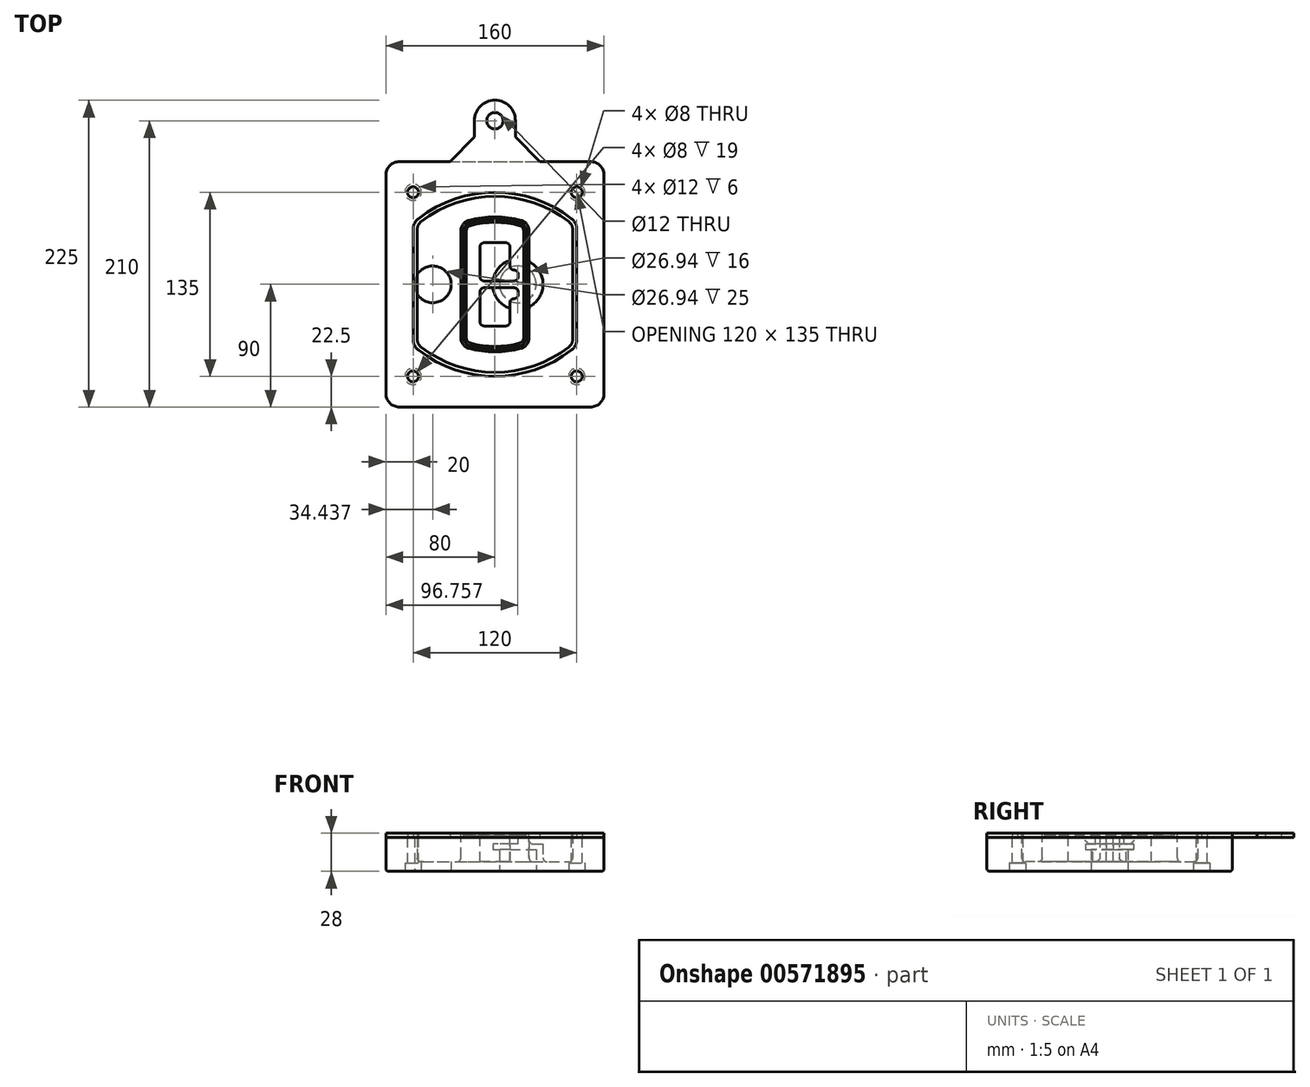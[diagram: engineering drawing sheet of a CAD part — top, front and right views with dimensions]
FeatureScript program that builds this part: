
annotation { "Feature Type Name" : "Feature", "Feature Type Description" : "" }
export const myFeature = defineFeature(function(context is Context, id is Id, definition is map)
    precondition{}
    {
        {
            var Q0;
            Q0=qCreatedBy(makeId("Top.planeOp"),FACE);
            var sketch = newSketch(context, id + "F0", { "sketchPlane" : qUnion([Q0])});
            skPoint(sketch, "E0.rect.middle", {"position": v(0, 0) * mm});
            skLineSegment(sketch, "E1.bottom", {"start": v(-70, -90) * mm, "end": v(70, -90) * mm});
            skLineSegment(sketch, "E1.top", {"start": v(-70, 90) * mm, "end": v(70, 90) * mm});
            skLineSegment(sketch, "E1.left", {"start": v(-80, -80) * mm, "end": v(-80, 80) * mm});
            skLineSegment(sketch, "E1.right", {"start": v(80, -80) * mm, "end": v(80, 80) * mm});
            skLineSegment(sketch, "E2", {"start": v(-80, 90) * mm, "end": v(80, -90) * mm, "construction": true});
            skLineSegment(sketch, "E3", {"start": v(80, 90) * mm, "end": v(-80, -90) * mm, "construction": true});
            skCircle(sketch, "E4", {"center": v(-60, 67.5) * mm, "radius": 4 * mm});
            skCircle(sketch, "E5", {"center": v(60, 67.5) * mm, "radius": 4 * mm});
            skCircle(sketch, "E6", {"center": v(60, -67.5) * mm, "radius": 4 * mm});
            skCircle(sketch, "E7", {"center": v(-60, -67.5) * mm, "radius": 4 * mm});
            skLineSegment(sketch, "E8", {"start": v(-60, 67.5) * mm, "end": v(60, 67.5) * mm, "construction": true});
            skLineSegment(sketch, "E9", {"start": v(60, 67.5) * mm, "end": v(60, -67.5) * mm, "construction": true});
            skLineSegment(sketch, "E10", {"start": v(60, -67.5) * mm, "end": v(-60, -67.5) * mm, "construction": true});
            skLineSegment(sketch, "E11", {"start": v(-60, -67.5) * mm, "end": v(-60, 67.5) * mm, "construction": true});
            skLineSegment(sketch, "E12", {"start": v(-60, 40.3) * mm, "end": v(-60, -40.3) * mm});
            skLineSegment(sketch, "E13", {"start": v(60, 40.3) * mm, "end": v(60, -40.3) * mm});
            skArc(sketch, "E14", {"start": v(56.15, 48.18) * mm, "mid": v(0, 67.5) * mm, "end": v(-56.15, 48.18) * mm});
            skArc(sketch, "E15", {"start": v(-56.15, -48.18) * mm, "mid": v(0, -67.5) * mm, "end": v(56.15, -48.18) * mm});
            skLineSegment(sketch, "E16", {"start": v(-60, 0) * mm, "end": v(60, 0) * mm, "construction": true});
            skPoint(sketch, "E17.visualSharp", {"position": v(-60, -45) * mm});
            skArc(sketch, "E17.filletArc", {"start": v(-60, -40.3) * mm, "mid": v(-58.99, -44.68) * mm, "end": v(-56.15, -48.18) * mm});
            skPoint(sketch, "E18.visualSharp", {"position": v(-60, 45) * mm});
            skArc(sketch, "E18.filletArc", {"start": v(-56.15, 48.18) * mm, "mid": v(-58.99, 44.68) * mm, "end": v(-60, 40.3) * mm});
            skPoint(sketch, "E19.visualSharp", {"position": v(60, 45) * mm});
            skArc(sketch, "E19.filletArc", {"start": v(60, 40.3) * mm, "mid": v(58.99, 44.68) * mm, "end": v(56.15, 48.18) * mm});
            skPoint(sketch, "E20.visualSharp", {"position": v(60, -45) * mm});
            skArc(sketch, "E20.filletArc", {"start": v(56.15, -48.18) * mm, "mid": v(58.99, -44.68) * mm, "end": v(60, -40.3) * mm});
            skPoint(sketch, "E21.visualSharp", {"position": v(-80, 90) * mm});
            skArc(sketch, "E21.filletArc", {"start": v(-70, 90) * mm, "mid": v(-77.07, 87.07) * mm, "end": v(-80, 80) * mm});
            skPoint(sketch, "E22.visualSharp", {"position": v(80, 90) * mm});
            skArc(sketch, "E22.filletArc", {"start": v(80, 80) * mm, "mid": v(77.07, 87.07) * mm, "end": v(70, 90) * mm});
            skPoint(sketch, "E23.visualSharp", {"position": v(80, -90) * mm});
            skArc(sketch, "E23.filletArc", {"start": v(70, -90) * mm, "mid": v(77.07, -87.07) * mm, "end": v(80, -80) * mm});
            skPoint(sketch, "E24.visualSharp", {"position": v(-80, -90) * mm});
            skArc(sketch, "E24.filletArc", {"start": v(-80, -80) * mm, "mid": v(-77.07, -87.07) * mm, "end": v(-70, -90) * mm});
            skArc(sketch, "E25.0", {"start": v(57, 40.3) * mm, "mid": v(56.3, 43.36) * mm, "end": v(54.3, 45.81) * mm});
            skLineSegment(sketch, "E25.1", {"start": v(57, 40.3) * mm, "end": v(57, -40.3) * mm});
            skArc(sketch, "E25.2", {"start": v(54.3, -45.81) * mm, "mid": v(56.3, -43.36) * mm, "end": v(57, -40.3) * mm});
            skArc(sketch, "E25.3", {"start": v(-54.3, -45.81) * mm, "mid": v(0, -64.5) * mm, "end": v(54.3, -45.81) * mm});
            skArc(sketch, "E25.4", {"start": v(-57, -40.3) * mm, "mid": v(-56.3, -43.36) * mm, "end": v(-54.3, -45.81) * mm});
            skArc(sketch, "E25.5", {"start": v(54.3, 45.81) * mm, "mid": v(0, 64.5) * mm, "end": v(-54.3, 45.81) * mm});
            skLineSegment(sketch, "E25.6", {"start": v(-57, 40.3) * mm, "end": v(-57, -40.3) * mm});
            skArc(sketch, "E25.7", {"start": v(-54.3, 45.81) * mm, "mid": v(-56.3, 43.36) * mm, "end": v(-57, 40.3) * mm});
            skArc(sketch, "E26.0", {"start": v(-58.62, 51.33) * mm, "mid": v(-62.58, 46.43) * mm, "end": v(-64, 40.3) * mm});
            skArc(sketch, "E26.1", {"start": v(58.62, 51.33) * mm, "mid": v(0, 71.5) * mm, "end": v(-58.62, 51.33) * mm});
            skArc(sketch, "E26.2", {"start": v(64, 40.3) * mm, "mid": v(62.58, 46.43) * mm, "end": v(58.62, 51.33) * mm});
            skLineSegment(sketch, "E26.3", {"start": v(64, 40.3) * mm, "end": v(64, -40.3) * mm});
            skArc(sketch, "E26.4", {"start": v(58.62, -51.33) * mm, "mid": v(62.58, -46.43) * mm, "end": v(64, -40.3) * mm});
            skLineSegment(sketch, "E26.5", {"start": v(-64, 40.3) * mm, "end": v(-64, -40.3) * mm});
            skArc(sketch, "E26.6", {"start": v(-58.62, -51.33) * mm, "mid": v(0, -71.5) * mm, "end": v(58.62, -51.33) * mm});
            skArc(sketch, "E26.7", {"start": v(-64, -40.3) * mm, "mid": v(-62.58, -46.43) * mm, "end": v(-58.62, -51.33) * mm});
            skSolve(sketch);
        }
        {
            var Q0;
            Q0=makeQuery(id+"F0.imprint","IMPRINT",FACE,{"disambiguationData":[TD([[makeQuery(id+"F0.imprint","IMPRINT",EDGE,{"derivedFrom":sQuery(id+"F0.wireOp",EDGE,"E1.bottom")}),1.0]])]});
            var Q1;
            Q1=makeQuery(id+"F0.imprint","IMPRINT",FACE,{"disambiguationData":[TD([[makeQuery(id+"F0.imprint","IMPRINT",EDGE,{"derivedFrom":sQuery(id+"F0.wireOp",EDGE,"E12")}),1.0]])]});
            var Q2;
            Q2=makeQuery(id+"F0.imprint","IMPRINT",FACE,{"disambiguationData":[TD([[makeQuery(id+"F0.imprint","IMPRINT",EDGE,{"derivedFrom":sQuery(id+"F0.wireOp",EDGE,"E25.0")}),1.0]])]});
            var Q3;
            Q3=makeQuery(id+"F0.imprint","IMPRINT",FACE,{"disambiguationData":[TD([[makeQuery(id+"F0.imprint","IMPRINT",EDGE,{"derivedFrom":sQuery(id+"F0.wireOp",EDGE,"E12")}),-1.0]])]});
            extrude(context, id + "F1", {"entities" : qUnion([Q0, Q1, Q2, Q3]), "oppositeDirection" : true, "depth" : 25 * mm});
        }
        {
            var Q0;
            Q0=makeQuery(id+"F0.imprint","IMPRINT",FACE,{"disambiguationData":[TD([[makeQuery(id+"F0.imprint","IMPRINT",EDGE,{"derivedFrom":sQuery(id+"F0.wireOp",EDGE,"E12")}),1.0]])]});
            extrude(context, id + "F2", {"entities" : qUnion([Q0]), "operationType" : NewBodyOperationType.ADD, "depth" : 3 * mm});
        }
        {
            var Q0;
            Q0=makeQuery(id+"F0.imprint","IMPRINT",FACE,{"disambiguationData":[TD([[makeQuery(id+"F0.imprint","IMPRINT",EDGE,{"derivedFrom":sQuery(id+"F0.wireOp",EDGE,"E25.0")}),1.0]])]});
            extrude(context, id + "F3", {"entities" : qUnion([Q0]), "operationType" : NewBodyOperationType.REMOVE, "oppositeDirection" : true, "depth" : 18 * mm});
        }
        {
            var Q0;
            Q0=makeQuery(id+"F2.opExtrude","CAP_FACE",FACE,{"disambiguationData":[OSD([sQuery(id+"F0.wireOp",EDGE,"E12"),sQuery(id+"F0.wireOp",EDGE,"E13"),sQuery(id+"F0.wireOp",EDGE,"E14"),sQuery(id+"F0.wireOp",EDGE,"E15"),sQuery(id+"F0.wireOp",EDGE,"E17.filletArc"),sQuery(id+"F0.wireOp",EDGE,"E18.filletArc"),sQuery(id+"F0.wireOp",EDGE,"E19.filletArc"),sQuery(id+"F0.wireOp",EDGE,"E20.filletArc"),sQuery(id+"F0.wireOp",EDGE,"E25.0"),sQuery(id+"F0.wireOp",EDGE,"E25.1"),sQuery(id+"F0.wireOp",EDGE,"E25.2"),sQuery(id+"F0.wireOp",EDGE,"E25.3"),sQuery(id+"F0.wireOp",EDGE,"E25.4"),sQuery(id+"F0.wireOp",EDGE,"E25.5"),sQuery(id+"F0.wireOp",EDGE,"E25.6"),sQuery(id+"F0.wireOp",EDGE,"E25.7")])],"isStart":false});
            var sketch = newSketch(context, id + "F4", { "sketchPlane" : qUnion([Q0])});
            skArc(sketch, "E27.0", {"start": v(-19.08, -46.97) * mm, "mid": v(0, -49.5) * mm, "end": v(19.08, -46.97) * mm});
            skArc(sketch, "E28.0", {"start": v(19.08, 46.97) * mm, "mid": v(0, 49.5) * mm, "end": v(-19.08, 46.97) * mm});
            skLineSegment(sketch, "E29", {"start": v(-25, 39.25) * mm, "end": v(-25, -39.25) * mm});
            skLineSegment(sketch, "E30", {"start": v(25, 39.25) * mm, "end": v(25, -39.25) * mm});
            skLineSegment(sketch, "E31", {"start": v(-25, 45.1) * mm, "end": v(25, 45.1) * mm, "construction": true});
            skLineSegment(sketch, "E32", {"start": v(-25, -45.1) * mm, "end": v(25, -45.1) * mm, "construction": true});
            skPoint(sketch, "E33.visualSharp", {"position": v(-25, 45.1) * mm});
            skArc(sketch, "E33.filletArc", {"start": v(-19.08, 46.97) * mm, "mid": v(-23.35, 44.11) * mm, "end": v(-25, 39.25) * mm});
            skPoint(sketch, "E34.visualSharp", {"position": v(25, 45.1) * mm});
            skArc(sketch, "E34.filletArc", {"start": v(25, 39.25) * mm, "mid": v(23.35, 44.11) * mm, "end": v(19.08, 46.97) * mm});
            skPoint(sketch, "E35.visualSharp", {"position": v(25, -45.1) * mm});
            skArc(sketch, "E35.filletArc", {"start": v(19.08, -46.97) * mm, "mid": v(23.35, -44.11) * mm, "end": v(25, -39.25) * mm});
            skPoint(sketch, "E36.visualSharp", {"position": v(-25, -45.1) * mm});
            skArc(sketch, "E36.filletArc", {"start": v(-25, -39.25) * mm, "mid": v(-23.35, -44.11) * mm, "end": v(-19.08, -46.97) * mm});
            skArc(sketch, "E37.0", {"start": v(54.3, 45.81) * mm, "mid": v(0, 64.5) * mm, "end": v(-54.3, 45.81) * mm});
            skArc(sketch, "E37.1", {"start": v(-54.3, 45.81) * mm, "mid": v(-56.3, 43.36) * mm, "end": v(-57, 40.3) * mm});
            skLineSegment(sketch, "E37.2", {"start": v(-57, 40.3) * mm, "end": v(-57, -40.3) * mm});
            skArc(sketch, "E37.3", {"start": v(-57, -40.3) * mm, "mid": v(-56.3, -43.36) * mm, "end": v(-54.3, -45.81) * mm});
            skArc(sketch, "E37.4", {"start": v(-54.3, -45.81) * mm, "mid": v(0, -64.5) * mm, "end": v(54.3, -45.81) * mm});
            skArc(sketch, "E37.5", {"start": v(54.3, -45.81) * mm, "mid": v(56.3, -43.36) * mm, "end": v(57, -40.3) * mm});
            skLineSegment(sketch, "E37.6", {"start": v(57, 40.3) * mm, "end": v(57, -40.3) * mm});
            skArc(sketch, "E37.7", {"start": v(57, 40.3) * mm, "mid": v(56.3, 43.36) * mm, "end": v(54.3, 45.81) * mm});
            skLineSegment(sketch, "E38.0", {"start": v(23, 39.25) * mm, "end": v(23, -39.25) * mm});
            skArc(sketch, "E38.1", {"start": v(18.56, -45.04) * mm, "mid": v(21.76, -42.9) * mm, "end": v(23, -39.25) * mm});
            skArc(sketch, "E38.2", {"start": v(-18.56, -45.04) * mm, "mid": v(0, -47.5) * mm, "end": v(18.56, -45.04) * mm});
            skArc(sketch, "E38.3", {"start": v(-23, -39.25) * mm, "mid": v(-21.76, -42.9) * mm, "end": v(-18.56, -45.04) * mm});
            skLineSegment(sketch, "E38.4", {"start": v(-23, 39.25) * mm, "end": v(-23, -39.25) * mm});
            skArc(sketch, "E38.5", {"start": v(23, 39.25) * mm, "mid": v(21.76, 42.9) * mm, "end": v(18.56, 45.04) * mm});
            skArc(sketch, "E38.6", {"start": v(-18.56, 45.04) * mm, "mid": v(-21.76, 42.9) * mm, "end": v(-23, 39.25) * mm});
            skArc(sketch, "E38.7", {"start": v(18.56, 45.04) * mm, "mid": v(0, 47.5) * mm, "end": v(-18.56, 45.04) * mm});
            skArc(sketch, "E39.0", {"start": v(21, 39.25) * mm, "mid": v(20.18, 41.68) * mm, "end": v(18.04, 43.1) * mm});
            skLineSegment(sketch, "E39.1", {"start": v(21, 39.25) * mm, "end": v(21, -39.25) * mm});
            skArc(sketch, "E39.2", {"start": v(18.04, -43.1) * mm, "mid": v(20.18, -41.68) * mm, "end": v(21, -39.25) * mm});
            skArc(sketch, "E39.3", {"start": v(-18.04, -43.1) * mm, "mid": v(0, -45.5) * mm, "end": v(18.04, -43.1) * mm});
            skArc(sketch, "E39.4", {"start": v(-21, -39.25) * mm, "mid": v(-20.18, -41.68) * mm, "end": v(-18.04, -43.1) * mm});
            skArc(sketch, "E39.5", {"start": v(18.04, 43.1) * mm, "mid": v(0, 45.5) * mm, "end": v(-18.04, 43.1) * mm});
            skLineSegment(sketch, "E39.6", {"start": v(-21, 39.25) * mm, "end": v(-21, -39.25) * mm});
            skArc(sketch, "E39.7", {"start": v(-18.04, 43.1) * mm, "mid": v(-20.18, 41.68) * mm, "end": v(-21, 39.25) * mm});
            skLineSegment(sketch, "E40", {"start": v(-25, 0) * mm, "end": v(25, 0) * mm, "construction": true});
            skLineSegment(sketch, "E41", {"start": v(-11, 5.5) * mm, "end": v(-11, 27.5) * mm});
            skLineSegment(sketch, "E42", {"start": v(-8, 30.5) * mm, "end": v(8, 30.5) * mm});
            skLineSegment(sketch, "E43", {"start": v(11, 27.5) * mm, "end": v(11, 13.5) * mm});
            skLineSegment(sketch, "E44", {"start": v(14, 10.5) * mm, "end": v(14, 10.5) * mm});
            skLineSegment(sketch, "E45", {"start": v(17, 7.5) * mm, "end": v(17, 5.5) * mm});
            skLineSegment(sketch, "E46", {"start": v(14, 2.5) * mm, "end": v(-8, 2.5) * mm});
            skPoint(sketch, "E47.visualSharp", {"position": v(-11, 30.5) * mm});
            skArc(sketch, "E47.filletArc", {"start": v(-8, 30.5) * mm, "mid": v(-10.12, 29.62) * mm, "end": v(-11, 27.5) * mm});
            skPoint(sketch, "E48.visualSharp", {"position": v(11, 30.5) * mm});
            skArc(sketch, "E48.filletArc", {"start": v(11, 27.5) * mm, "mid": v(10.12, 29.62) * mm, "end": v(8, 30.5) * mm});
            skPoint(sketch, "E49.visualSharp", {"position": v(11, 10.5) * mm});
            skArc(sketch, "E49.filletArc", {"start": v(11, 13.5) * mm, "mid": v(11.88, 11.38) * mm, "end": v(14, 10.5) * mm});
            skPoint(sketch, "E50.visualSharp", {"position": v(17, 10.5) * mm});
            skArc(sketch, "E50.filletArc", {"start": v(17, 7.5) * mm, "mid": v(16.12, 9.62) * mm, "end": v(14, 10.5) * mm});
            skPoint(sketch, "E51.visualSharp", {"position": v(17, 2.5) * mm});
            skArc(sketch, "E51.filletArc", {"start": v(14, 2.5) * mm, "mid": v(16.12, 3.38) * mm, "end": v(17, 5.5) * mm});
            skPoint(sketch, "E52.visualSharp", {"position": v(-11, 2.5) * mm});
            skArc(sketch, "E52.filletArc", {"start": v(-11, 5.5) * mm, "mid": v(-10.12, 3.38) * mm, "end": v(-8, 2.5) * mm});
            skLineSegment(sketch, "E53.0.MirrorCS", {"start": v(14, -2.5) * mm, "end": v(-8, -2.5) * mm});
            skArc(sketch, "E54.0.MirrorCS", {"start": v(-11, -5.5) * mm, "mid": v(-10.12, -3.38) * mm, "end": v(-8, -2.5) * mm});
            skLineSegment(sketch, "E55.0.MirrorCS", {"start": v(-11, -5.5) * mm, "end": v(-11, -27.5) * mm});
            skArc(sketch, "E56.0.MirrorCS", {"start": v(-8, -30.5) * mm, "mid": v(-10.12, -29.62) * mm, "end": v(-11, -27.5) * mm});
            skLineSegment(sketch, "E57.0.MirrorCS", {"start": v(-8, -30.5) * mm, "end": v(8, -30.5) * mm});
            skArc(sketch, "E58.0.MirrorCS", {"start": v(11, -27.5) * mm, "mid": v(10.12, -29.62) * mm, "end": v(8, -30.5) * mm});
            skLineSegment(sketch, "E59.0.MirrorCS", {"start": v(11, -27.5) * mm, "end": v(11, -13.5) * mm});
            skArc(sketch, "E60.0.MirrorCS", {"start": v(11, -13.5) * mm, "mid": v(11.88, -11.38) * mm, "end": v(14, -10.5) * mm});
            skArc(sketch, "E61.0.MirrorCS", {"start": v(17, -7.5) * mm, "mid": v(16.12, -9.62) * mm, "end": v(14, -10.5) * mm});
            skLineSegment(sketch, "E62.0.MirrorCS", {"start": v(17, -7.5) * mm, "end": v(17, -5.5) * mm});
            skArc(sketch, "E63.0.MirrorCS", {"start": v(14, -2.5) * mm, "mid": v(16.12, -3.38) * mm, "end": v(17, -5.5) * mm});
            skSolve(sketch);
        }
        {
            var Q0;
            Q0=makeQuery(id+"F4.imprint","IMPRINT",FACE,{"disambiguationData":[TD([[makeQuery(id+"F4.imprint","IMPRINT",EDGE,{"derivedFrom":sQuery(id+"F4.wireOp",EDGE,"E27.0")}),1.0]])]});
            var Q1;
            Q1=makeQuery(id+"F4.imprint","IMPRINT",FACE,{"disambiguationData":[TD([[makeQuery(id+"F4.imprint","IMPRINT",EDGE,{"derivedFrom":sQuery(id+"F4.wireOp",EDGE,"E38.0")}),-1.0]])]});
            var Q2;
            Q2=makeQuery(id+"F4.imprint","IMPRINT",FACE,{"disambiguationData":[TD([[makeQuery(id+"F4.imprint","IMPRINT",EDGE,{"derivedFrom":sQuery(id+"F4.wireOp",EDGE,"E39.0")}),1.0]])]});
            extrude(context, id + "F5", {"entities" : qUnion([Q0, Q1, Q2]), "operationType" : NewBodyOperationType.ADD, "endBound" : BoundingType.UP_TO_NEXT, "oppositeDirection" : true, "depth" : 25 * mm});
        }
        {
            var Q0;
            Q0=makeQuery(id+"F4.imprint","IMPRINT",FACE,{"disambiguationData":[TD([[makeQuery(id+"F4.imprint","IMPRINT",EDGE,{"derivedFrom":sQuery(id+"F4.wireOp",EDGE,"E38.0")}),-1.0]])]});
            extrude(context, id + "F6", {"entities" : qUnion([Q0]), "operationType" : NewBodyOperationType.REMOVE, "oppositeDirection" : true, "depth" : 2 * mm});
        }
        {
            var Q0;
            Q0=makeQuery(id+"F1.opExtrude","CAP_FACE",FACE,{"disambiguationData":[OSD([sQuery(id+"F0.wireOp",EDGE,"E1.bottom"),sQuery(id+"F0.wireOp",EDGE,"E1.top"),sQuery(id+"F0.wireOp",EDGE,"E1.left"),sQuery(id+"F0.wireOp",EDGE,"E1.right"),sQuery(id+"F0.wireOp",EDGE,"E4"),sQuery(id+"F0.wireOp",EDGE,"E5"),sQuery(id+"F0.wireOp",EDGE,"E6"),sQuery(id+"F0.wireOp",EDGE,"E7"),sQuery(id+"F0.wireOp",EDGE,"E21.filletArc"),sQuery(id+"F0.wireOp",EDGE,"E22.filletArc"),sQuery(id+"F0.wireOp",EDGE,"E23.filletArc"),sQuery(id+"F0.wireOp",EDGE,"E24.filletArc")])],"isStart":false});
            var sketch = newSketch(context, id + "F7", { "sketchPlane" : qUnion([Q0])});
            skCircle(sketch, "E64", {"center": v(16.76, 0) * mm, "radius": 13.47 * mm});
            skCircle(sketch, "E65", {"center": v(-45.56, 0) * mm, "radius": 13.47 * mm});
            skLineSegment(sketch, "E66", {"start": v(80, 0) * mm, "end": v(-80, 0) * mm});
            skCircle(sketch, "E67", {"center": v(16.76, 0) * mm, "radius": 18.47 * mm});
            skCircle(sketch, "E68", {"center": v(60, -67.5) * mm, "radius": 6 * mm});
            skCircle(sketch, "E69", {"center": v(-60, -67.5) * mm, "radius": 6 * mm});
            skCircle(sketch, "E70", {"center": v(-60, 67.5) * mm, "radius": 6 * mm});
            skCircle(sketch, "E71", {"center": v(60, 67.5) * mm, "radius": 6 * mm});
            skSolve(sketch);
        }
        {
            var Q0;
            {var subQ1=sQuery(id+"F7.wireOp",EDGE,"E66");var subQ4=sQuery(id+"F7.wireOp",EDGE,"E64");var subQ6=makeQuery(id+"F7.imprint","INTERSECT",VERTEX,{"disambiguationData":[OD(0.0)],"derivedFrom":[subQ4,subQ1]});Q0=makeQuery(id+"F7.imprint","IMPRINT",FACE,{"disambiguationData":[TD([[makeQuery(id+"F7.imprint","IMPRINT",EDGE,{"disambiguationData":[TD([[subQ6,-1.0]])],"derivedFrom":subQ4}),-1.0]])]});}
            var Q1;
            {var subQ0=sQuery(id+"F7.wireOp",EDGE,"E66");var subQ1=sQuery(id+"F7.wireOp",EDGE,"E64");var subQ3=makeQuery(id+"F7.imprint","INTERSECT",VERTEX,{"disambiguationData":[OD(0.0)],"derivedFrom":[subQ1,subQ0]});Q1=makeQuery(id+"F7.imprint","IMPRINT",FACE,{"disambiguationData":[TD([[makeQuery(id+"F7.imprint","IMPRINT",EDGE,{"disambiguationData":[TD([[subQ3,-1.0]])],"derivedFrom":subQ1}),1.0]])]});}
            var Q2;
            {var subQ0=sQuery(id+"F7.wireOp",EDGE,"E66");var subQ1=sQuery(id+"F7.wireOp",EDGE,"E64");var subQ3=makeQuery(id+"F7.imprint","INTERSECT",VERTEX,{"disambiguationData":[OD(0.0)],"derivedFrom":[subQ1,subQ0]});Q2=makeQuery(id+"F7.imprint","IMPRINT",FACE,{"disambiguationData":[TD([[makeQuery(id+"F7.imprint","IMPRINT",EDGE,{"disambiguationData":[TD([[subQ3,1.0]])],"derivedFrom":subQ1}),1.0]])]});}
            var Q3;
            {var subQ1=sQuery(id+"F7.wireOp",EDGE,"E66");var subQ4=sQuery(id+"F7.wireOp",EDGE,"E64");var subQ6=makeQuery(id+"F7.imprint","INTERSECT",VERTEX,{"disambiguationData":[OD(0.0)],"derivedFrom":[subQ4,subQ1]});Q3=makeQuery(id+"F7.imprint","IMPRINT",FACE,{"disambiguationData":[TD([[makeQuery(id+"F7.imprint","IMPRINT",EDGE,{"disambiguationData":[TD([[subQ6,1.0]])],"derivedFrom":subQ4}),-1.0]])]});}
            extrude(context, id + "F8", {"entities" : qUnion([Q0, Q1, Q2, Q3]), "operationType" : NewBodyOperationType.ADD, "oppositeDirection" : true, "depth" : 20 * mm});
        }
        {
            var Q0;
            {var subQ0=sQuery(id+"F7.wireOp",EDGE,"E66");var subQ1=sQuery(id+"F7.wireOp",EDGE,"E64");var subQ3=makeQuery(id+"F7.imprint","INTERSECT",VERTEX,{"disambiguationData":[OD(0.0)],"derivedFrom":[subQ1,subQ0]});Q0=makeQuery(id+"F7.imprint","IMPRINT",FACE,{"disambiguationData":[TD([[makeQuery(id+"F7.imprint","IMPRINT",EDGE,{"disambiguationData":[TD([[subQ3,-1.0]])],"derivedFrom":subQ1}),1.0]])]});}
            var Q1;
            {var subQ0=sQuery(id+"F7.wireOp",EDGE,"E66");var subQ1=sQuery(id+"F7.wireOp",EDGE,"E64");var subQ3=makeQuery(id+"F7.imprint","INTERSECT",VERTEX,{"disambiguationData":[OD(0.0)],"derivedFrom":[subQ1,subQ0]});Q1=makeQuery(id+"F7.imprint","IMPRINT",FACE,{"disambiguationData":[TD([[makeQuery(id+"F7.imprint","IMPRINT",EDGE,{"disambiguationData":[TD([[subQ3,1.0]])],"derivedFrom":subQ1}),1.0]])]});}
            extrude(context, id + "F9", {"entities" : qUnion([Q0, Q1]), "operationType" : NewBodyOperationType.REMOVE, "oppositeDirection" : true, "depth" : 16 * mm});
        }
        {
            var Q0;
            {var subQ0=sQuery(id+"F7.wireOp",EDGE,"E66");var subQ1=sQuery(id+"F7.wireOp",EDGE,"E65");var subQ3=makeQuery(id+"F7.imprint","INTERSECT",VERTEX,{"disambiguationData":[OD(0.0)],"derivedFrom":[subQ1,subQ0]});Q0=makeQuery(id+"F7.imprint","IMPRINT",FACE,{"disambiguationData":[TD([[makeQuery(id+"F7.imprint","IMPRINT",EDGE,{"disambiguationData":[TD([[subQ3,-1.0]])],"derivedFrom":subQ1}),1.0]])]});}
            var Q1;
            {var subQ0=sQuery(id+"F7.wireOp",EDGE,"E66");var subQ1=sQuery(id+"F7.wireOp",EDGE,"E65");var subQ3=makeQuery(id+"F7.imprint","INTERSECT",VERTEX,{"disambiguationData":[OD(0.0)],"derivedFrom":[subQ1,subQ0]});Q1=makeQuery(id+"F7.imprint","IMPRINT",FACE,{"disambiguationData":[TD([[makeQuery(id+"F7.imprint","IMPRINT",EDGE,{"disambiguationData":[TD([[subQ3,1.0]])],"derivedFrom":subQ1}),1.0]])]});}
            extrude(context, id + "F10", {"entities" : qUnion([Q0, Q1]), "operationType" : NewBodyOperationType.REMOVE, "oppositeDirection" : true, "depth" : 25 * mm});
        }
        {
            var Q0;
            Q0=makeQuery(id+"F7.imprint","IMPRINT",FACE,{"disambiguationData":[TD([[makeQuery(id+"F7.imprint","IMPRINT",EDGE,{"derivedFrom":sQuery(id+"F7.wireOp",EDGE,"E68")}),1.0]])]});
            var Q1;
            Q1=makeQuery(id+"F7.imprint","IMPRINT",FACE,{"disambiguationData":[TD([[makeQuery(id+"F7.imprint","IMPRINT",EDGE,{"derivedFrom":makeQuery(id+"F1.opExtrude","CAP_EDGE",EDGE,{"disambiguationData":[OSD([sQuery(id+"F0.wireOp",EDGE,"E5")])],"isStart":false})}),-1.0]])]});
            var Q2;
            Q2=makeQuery(id+"F7.imprint","IMPRINT",FACE,{"disambiguationData":[TD([[makeQuery(id+"F7.imprint","IMPRINT",EDGE,{"derivedFrom":sQuery(id+"F7.wireOp",EDGE,"E69")}),1.0]])]});
            var Q3;
            Q3=makeQuery(id+"F7.imprint","IMPRINT",FACE,{"disambiguationData":[TD([[makeQuery(id+"F7.imprint","IMPRINT",EDGE,{"derivedFrom":makeQuery(id+"F1.opExtrude","CAP_EDGE",EDGE,{"disambiguationData":[OSD([sQuery(id+"F0.wireOp",EDGE,"E4")])],"isStart":false})}),-1.0]])]});
            var Q4;
            Q4=makeQuery(id+"F7.imprint","IMPRINT",FACE,{"disambiguationData":[TD([[makeQuery(id+"F7.imprint","IMPRINT",EDGE,{"derivedFrom":sQuery(id+"F7.wireOp",EDGE,"E70")}),1.0]])]});
            var Q5;
            Q5=makeQuery(id+"F7.imprint","IMPRINT",FACE,{"disambiguationData":[TD([[makeQuery(id+"F7.imprint","IMPRINT",EDGE,{"derivedFrom":makeQuery(id+"F1.opExtrude","CAP_EDGE",EDGE,{"disambiguationData":[OSD([sQuery(id+"F0.wireOp",EDGE,"E7")])],"isStart":false})}),-1.0]])]});
            var Q6;
            Q6=makeQuery(id+"F7.imprint","IMPRINT",FACE,{"disambiguationData":[TD([[makeQuery(id+"F7.imprint","IMPRINT",EDGE,{"derivedFrom":sQuery(id+"F7.wireOp",EDGE,"E71")}),1.0]])]});
            var Q7;
            Q7=makeQuery(id+"F7.imprint","IMPRINT",FACE,{"disambiguationData":[TD([[makeQuery(id+"F7.imprint","IMPRINT",EDGE,{"derivedFrom":makeQuery(id+"F1.opExtrude","CAP_EDGE",EDGE,{"disambiguationData":[OSD([sQuery(id+"F0.wireOp",EDGE,"E6")])],"isStart":false})}),-1.0]])]});
            extrude(context, id + "F11", {"entities" : qUnion([Q0, Q1, Q2, Q3, Q4, Q5, Q6, Q7]), "operationType" : NewBodyOperationType.REMOVE, "oppositeDirection" : true, "depth" : 6 * mm});
        }
        {
            var Q0;
            Q0=makeQuery(id+"F9.boolean.opBoolean","COPY",FACE,{"derivedFrom":makeQuery(id+"F9.opExtrude","CAP_FACE",FACE,{"disambiguationData":[OSD([sQuery(id+"F7.wireOp",EDGE,"E64")])],"isStart":false})});
            var sketch = newSketch(context, id + "F12", { "sketchPlane" : qUnion([Q0])});
            skArc(sketch, "E72.0", {"start": v(11, 17.55) * mm, "mid": v(2.57, 11.82) * mm, "end": v(-1.54, 2.5) * mm});
            skArc(sketch, "E72.1", {"start": v(-1.54, -2.5) * mm, "mid": v(2.57, -11.82) * mm, "end": v(11, -17.55) * mm});
            skLineSegment(sketch, "E73", {"start": v(-1.54, -2.5) * mm, "end": v(14, -2.5) * mm});
            skLineSegment(sketch, "E74.0", {"start": v(14, 2.5) * mm, "end": v(-1.54, 2.5) * mm});
            skArc(sketch, "E74.1", {"start": v(14, 2.5) * mm, "mid": v(16.12, 3.38) * mm, "end": v(17, 5.5) * mm});
            skLineSegment(sketch, "E74.2", {"start": v(17, 7.5) * mm, "end": v(17, 5.5) * mm});
            skArc(sketch, "E74.3", {"start": v(17, 7.5) * mm, "mid": v(16.12, 9.62) * mm, "end": v(14, 10.5) * mm});
            skArc(sketch, "E74.4", {"start": v(11, 13.5) * mm, "mid": v(11.88, 11.38) * mm, "end": v(14, 10.5) * mm});
            skLineSegment(sketch, "E74.5", {"start": v(11, 17.55) * mm, "end": v(11, 13.5) * mm});
            skLineSegment(sketch, "E74.7", {"start": v(14, -2.5) * mm, "end": v(-1.54, -2.5) * mm});
            skArc(sketch, "E74.8", {"start": v(14, -2.5) * mm, "mid": v(16.12, -3.38) * mm, "end": v(17, -5.5) * mm});
            skLineSegment(sketch, "E74.9", {"start": v(17, -7.5) * mm, "end": v(17, -5.5) * mm});
            skArc(sketch, "E74.10", {"start": v(17, -7.5) * mm, "mid": v(16.12, -9.62) * mm, "end": v(14, -10.5) * mm});
            skArc(sketch, "E74.11", {"start": v(11, -13.5) * mm, "mid": v(11.88, -11.38) * mm, "end": v(14, -10.5) * mm});
            skLineSegment(sketch, "E74.12", {"start": v(11, -17.55) * mm, "end": v(11, -13.5) * mm});
            skPoint(sketch, "E75.orphan", {"position": v(11, -27.5) * mm});
            skPoint(sketch, "E76.orphan", {"position": v(-8, -2.5) * mm});
            skPoint(sketch, "E77.orphan", {"position": v(-8, 2.5) * mm});
            skPoint(sketch, "E78.orphan", {"position": v(11, 27.5) * mm});
            skSolve(sketch);
        }
        {
            var Q0;
            {var subQ7=sQuery(id+"F12.wireOp",EDGE,"E72.0");var subQ14=sQuery(id+"F12.wireOp",EDGE,"E72.1");var subQ16=sQuery(id+"F12.wireOp",EDGE,"E74.1");var subQ18=sQuery(id+"F12.wireOp",EDGE,"E74.8");Q0=qUnion([makeQuery(id+"F12.imprint","IMPRINT",FACE,{"disambiguationData":[TD([[makeQuery(id+"F12.imprint","IMPRINT",EDGE,{"derivedFrom":subQ7}),1.0]])]}),makeQuery(id+"F12.imprint","IMPRINT",FACE,{"disambiguationData":[TD([[makeQuery(id+"F12.imprint","IMPRINT",EDGE,{"derivedFrom":subQ14}),1.0]])]}),makeQuery(id+"F12.imprint","IMPRINT",FACE,{"disambiguationData":[TD([[makeQuery(id+"F12.imprint","IMPRINT",EDGE,{"derivedFrom":subQ16}),1.0]])]}),makeQuery(id+"F12.imprint","IMPRINT",FACE,{"disambiguationData":[TD([[makeQuery(id+"F12.imprint","IMPRINT",EDGE,{"derivedFrom":subQ18}),-1.0]])]})]);}
            var Q1;
            Q1=makeQuery(id+"F5.boolean.opBoolean","SPLIT",FACE,{"disambiguationData":[TD([makeQuery(id+"F5.opExtrude","SWEPT_FACE",FACE,{"disambiguationData":[OSD([sQuery(id+"F4.wireOp",EDGE,"E41")])]})])],"derivedFrom":makeQuery(id+"F3.boolean.opBoolean","COPY",FACE,{"derivedFrom":makeQuery(id+"F3.opExtrude","CAP_FACE",FACE,{"disambiguationData":[OSD([sQuery(id+"F0.wireOp",EDGE,"E25.0"),sQuery(id+"F0.wireOp",EDGE,"E25.1"),sQuery(id+"F0.wireOp",EDGE,"E25.2"),sQuery(id+"F0.wireOp",EDGE,"E25.3"),sQuery(id+"F0.wireOp",EDGE,"E25.4"),sQuery(id+"F0.wireOp",EDGE,"E25.5"),sQuery(id+"F0.wireOp",EDGE,"E25.6"),sQuery(id+"F0.wireOp",EDGE,"E25.7")])],"isStart":false})})});
            extrude(context, id + "F13", {"entities" : qUnion([Q0]), "operationType" : NewBodyOperationType.REMOVE, "endBound" : BoundingType.UP_TO_SURFACE, "endBoundEntityFace" : qUnion([Q1]), "depth" : 25 * mm});
        }
        {
            var Q0;
            Q0=makeQuery(id+"F3.boolean.opBoolean","COPY",EDGE,{"derivedFrom":makeQuery(id+"F3.opExtrude","CAP_EDGE",EDGE,{"disambiguationData":[OSD([sQuery(id+"F0.wireOp",EDGE,"E25.6")])],"isStart":false})});
            var Q1;
            Q1=makeQuery(id+"F8.boolean.opBoolean","INTERSECT",EDGE,{"derivedFrom":[makeQuery(id+"F5.opExtrude","SWEPT_FACE",FACE,{"disambiguationData":[OSD([sQuery(id+"F4.wireOp",EDGE,"E30")])]}),makeQuery(id+"F8.opExtrude","CAP_FACE",FACE,{"disambiguationData":[OSD([sQuery(id+"F7.wireOp",EDGE,"E67")])],"isStart":false})]});
            var Q2;
            Q2=makeQuery(id+"F8.boolean.opBoolean","INTERSECT",EDGE,{"disambiguationData":[OD(1.0)],"derivedFrom":[makeQuery(id+"F5.opExtrude","SWEPT_FACE",FACE,{"disambiguationData":[OSD([sQuery(id+"F4.wireOp",EDGE,"E30")])]}),makeQuery(id+"F8.opExtrude","SWEPT_FACE",FACE,{"disambiguationData":[OSD([sQuery(id+"F7.wireOp",EDGE,"E67")])]})]});
            var Q3;
            {var subQ0=sQuery(id+"F4.wireOp",EDGE,"E30");Q3=makeQuery(id+"F8.boolean.opBoolean","SPLIT",EDGE,{"disambiguationData":[TD([makeQuery(id+"F5.opExtrude","SWEPT_FACE",FACE,{"disambiguationData":[OSD([sQuery(id+"F4.wireOp",EDGE,"E35.filletArc")])]})])],"derivedFrom":makeQuery(id+"F5.opExtrude","CAP_EDGE",EDGE,{"disambiguationData":[OSD([subQ0])],"isStart":false})});}
            var Q4;
            {var subQ0=sQuery(id+"F0.wireOp",EDGE,"E25.7");var subQ1=sQuery(id+"F0.wireOp",EDGE,"E25.1");var subQ2=sQuery(id+"F0.wireOp",EDGE,"E25.6");var subQ3=sQuery(id+"F0.wireOp",EDGE,"E25.5");var subQ4=sQuery(id+"F0.wireOp",EDGE,"E25.4");var subQ5=sQuery(id+"F0.wireOp",EDGE,"E25.0");var subQ6=sQuery(id+"F0.wireOp",EDGE,"E25.2");var subQ7=sQuery(id+"F0.wireOp",EDGE,"E25.3");Q4=makeQuery(id+"F8.boolean.opBoolean","INTERSECT",EDGE,{"derivedFrom":[makeQuery(id+"F5.boolean.opBoolean","SPLIT",FACE,{"disambiguationData":[TD([makeQuery(id+"F2.opExtrude","SWEPT_FACE",FACE,{"disambiguationData":[OSD([subQ5])]})])],"derivedFrom":makeQuery(id+"F3.boolean.opBoolean","COPY",FACE,{"derivedFrom":makeQuery(id+"F3.opExtrude","CAP_FACE",FACE,{"disambiguationData":[OSD([subQ5,subQ1,subQ6,subQ7,subQ4,subQ3,subQ2,subQ0])],"isStart":false})})}),makeQuery(id+"F8.opExtrude","SWEPT_FACE",FACE,{"disambiguationData":[OSD([sQuery(id+"F7.wireOp",EDGE,"E67")])]})]});}
            var Q5;
            Q5=makeQuery(id+"F8.boolean.opBoolean","INTERSECT",EDGE,{"disambiguationData":[OD(0.0)],"derivedFrom":[makeQuery(id+"F5.opExtrude","SWEPT_FACE",FACE,{"disambiguationData":[OSD([sQuery(id+"F4.wireOp",EDGE,"E30")])]}),makeQuery(id+"F8.opExtrude","SWEPT_FACE",FACE,{"disambiguationData":[OSD([sQuery(id+"F7.wireOp",EDGE,"E67")])]})]});
            fillet(context, id + "F14", {"entities" : qUnion([Q0, Q1, Q2, Q3, Q4, Q5]), "radius" : 3 * mm, "tangentPropagation" : true, "allowEdgeOverflow" : false});
        }
        {
            var Q0;
            Q0=makeQuery(id+"F1.opExtrude","CAP_EDGE",EDGE,{"disambiguationData":[OSD([sQuery(id+"F0.wireOp",EDGE,"E1.bottom")])],"isStart":false});
            fillet(context, id + "F15", {"entities" : qUnion([Q0]), "radius" : 2 * mm, "tangentPropagation" : true, "allowEdgeOverflow" : false});
        }
        {
            var Q0;
            {var subQ0=sQuery(id+"F0.wireOp",EDGE,"E21.filletArc");var subQ1=sQuery(id+"F0.wireOp",EDGE,"E7");var subQ2=sQuery(id+"F0.wireOp",EDGE,"E6");var subQ3=sQuery(id+"F0.wireOp",EDGE,"E5");var subQ4=sQuery(id+"F0.wireOp",EDGE,"E4");var subQ5=sQuery(id+"F0.wireOp",EDGE,"E22.filletArc");var subQ6=sQuery(id+"F0.wireOp",EDGE,"E1.bottom");var subQ7=sQuery(id+"F0.wireOp",EDGE,"E1.right");var subQ8=sQuery(id+"F0.wireOp",EDGE,"E1.top");var subQ9=sQuery(id+"F0.wireOp",EDGE,"E1.left");var subQ10=sQuery(id+"F0.wireOp",EDGE,"E23.filletArc");var subQ11=sQuery(id+"F0.wireOp",EDGE,"E24.filletArc");Q0=makeQuery(id+"F2.boolean.opBoolean","SPLIT",FACE,{"disambiguationData":[TD([makeQuery(id+"F1.opExtrude","SWEPT_FACE",FACE,{"disambiguationData":[OSD([subQ6])]})])],"derivedFrom":makeQuery(id+"F1.opExtrude","CAP_FACE",FACE,{"disambiguationData":[OSD([subQ6,subQ8,subQ9,subQ7,subQ4,subQ3,subQ2,subQ1,subQ0,subQ5,subQ10,subQ11])],"isStart":true})});}
            var sketch = newSketch(context, id + "F16", { "sketchPlane" : qUnion([Q0])});
            skLineSegment(sketch, "E79", {"start": v(0, 90) * mm, "end": v(0, 120) * mm, "construction": true});
            skPoint(sketch, "E79.endSnap0", {"position": v(0, 90) * mm});
            skLineSegment(sketch, "E80", {"start": v(-15, 120) * mm, "end": v(-15, 108) * mm});
            skLineSegment(sketch, "E81", {"start": v(15, 120) * mm, "end": v(15, 108) * mm});
            skLineSegment(sketch, "E82", {"start": v(-15, 108) * mm, "end": v(-33, 90) * mm});
            skLineSegment(sketch, "E83", {"start": v(15, 108) * mm, "end": v(33, 90) * mm});
            skArc(sketch, "E84", {"start": v(15, 120) * mm, "mid": v(0, 135) * mm, "end": v(-15, 120) * mm});
            skCircle(sketch, "E85", {"center": v(0, 120) * mm, "radius": 6 * mm});
            skLineSegment(sketch, "E86", {"start": v(-80, 0) * mm, "end": v(80, 0) * mm, "construction": true});
            skArc(sketch, "E87.MirrorCS", {"start": v(15, -120) * mm, "mid": v(0, -135) * mm, "end": v(-15, -120) * mm});
            skCircle(sketch, "E88.MirrorC", {"center": v(0, -120) * mm, "radius": 6 * mm});
            skLineSegment(sketch, "E89.MirrorCS", {"start": v(-15, -120) * mm, "end": v(-15, -108) * mm});
            skLineSegment(sketch, "E90.MirrorCS", {"start": v(15, -120) * mm, "end": v(15, -108) * mm});
            skLineSegment(sketch, "E91.MirrorCS", {"start": v(0, -90) * mm, "end": v(0, -120) * mm, "construction": true});
            skLineSegment(sketch, "E92.MirrorCS", {"start": v(15, -108) * mm, "end": v(33, -90) * mm});
            skLineSegment(sketch, "E93.MirrorCS", {"start": v(-15, -108) * mm, "end": v(-33, -90) * mm});
            skPoint(sketch, "E94.MirrorP", {"position": v(0, -90) * mm});
            skSolve(sketch);
        }
        {
            var Q0;
            Q0=makeQuery(id+"F16.imprint","IMPRINT",FACE,{"disambiguationData":[TD([[makeQuery(id+"F16.imprint","IMPRINT",EDGE,{"derivedFrom":sQuery(id+"F16.wireOp",EDGE,"E87.MirrorCS")}),-1.0]])]});
            var Q1;
            Q1=makeQuery(id+"F16.imprint","IMPRINT",FACE,{"disambiguationData":[TD([[makeQuery(id+"F16.imprint","IMPRINT",EDGE,{"derivedFrom":makeQuery(id+"F1.opExtrude","CAP_EDGE",EDGE,{"disambiguationData":[OSD([sQuery(id+"F0.wireOp",EDGE,"E1.left")])],"isStart":true})}),-1.0]])]});
            var Q2;
            Q2=makeQuery(id+"F16.imprint","IMPRINT",FACE,{"disambiguationData":[TD([[makeQuery(id+"F16.imprint","IMPRINT",EDGE,{"derivedFrom":sQuery(id+"F16.wireOp",EDGE,"E80")}),1.0]])]});
            var Q3;
            Q3=makeQuery(id+"F2.opExtrude","CAP_FACE",FACE,{"disambiguationData":[OSD([sQuery(id+"F0.wireOp",EDGE,"E12"),sQuery(id+"F0.wireOp",EDGE,"E13"),sQuery(id+"F0.wireOp",EDGE,"E14"),sQuery(id+"F0.wireOp",EDGE,"E15"),sQuery(id+"F0.wireOp",EDGE,"E17.filletArc"),sQuery(id+"F0.wireOp",EDGE,"E18.filletArc"),sQuery(id+"F0.wireOp",EDGE,"E19.filletArc"),sQuery(id+"F0.wireOp",EDGE,"E20.filletArc"),sQuery(id+"F0.wireOp",EDGE,"E25.0"),sQuery(id+"F0.wireOp",EDGE,"E25.1"),sQuery(id+"F0.wireOp",EDGE,"E25.2"),sQuery(id+"F0.wireOp",EDGE,"E25.3"),sQuery(id+"F0.wireOp",EDGE,"E25.4"),sQuery(id+"F0.wireOp",EDGE,"E25.5"),sQuery(id+"F0.wireOp",EDGE,"E25.6"),sQuery(id+"F0.wireOp",EDGE,"E25.7")])],"isStart":false});
            extrude(context, id + "F17", {"entities" : qUnion([Q0, Q1, Q2]), "endBound" : BoundingType.UP_TO_SURFACE, "depth" : 25 * mm, "endBoundEntityFace" : qUnion([Q3]), "offsetDistance" : 25 * mm});
        }
    });
